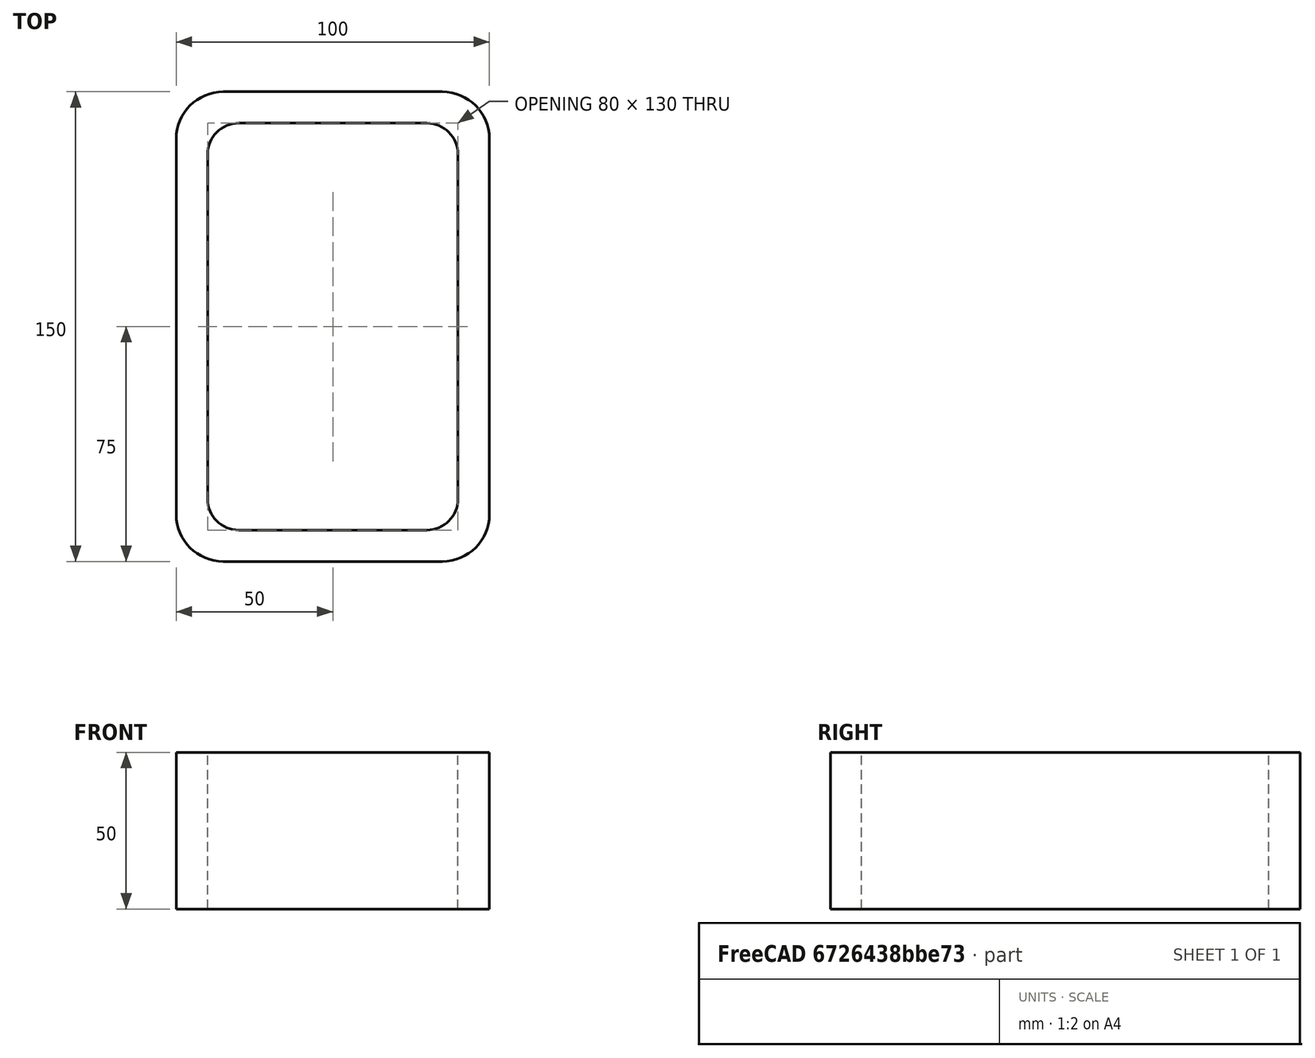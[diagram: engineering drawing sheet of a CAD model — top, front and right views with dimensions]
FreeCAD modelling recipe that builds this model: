
FCSTD DOCUMENT  (FreeCAD 0.15R4671 (Git))
Label: Rectangular hollow section 150x100x10 EN10219 S235JRH
License: All rights reserved
LicenseURL: http://en.wikipedia.org/wiki/All_rights_reserved
objects: Sketcher::SketchObject×1, Part::Extrusion×1
note: 2 computed .brp shape members not serialized (recipe doc carries the construction recipe); baked Part::Feature solids carry a one-line shape summary decoded from their .brp

FEATURE [Sketcher::SketchObject] Sketch
  sketch-geometry (16):
    g0: LineSegment StartX=-30 StartY=65 StartZ=0 EndX=30 EndY=65 EndZ=0
    g1: LineSegment StartX=40 StartY=55 StartZ=0 EndX=40 EndY=-55 EndZ=0
    g2: LineSegment StartX=30 StartY=-65 StartZ=0 EndX=-30 EndY=-65 EndZ=0
    g3: LineSegment StartX=-40 StartY=-55 StartZ=0 EndX=-40 EndY=55 EndZ=0
    g4: LineSegment StartX=-35 StartY=75 StartZ=0 EndX=35 EndY=75 EndZ=0
    g5: LineSegment StartX=50 StartY=60 StartZ=0 EndX=50 EndY=-60 EndZ=0
    g6: LineSegment StartX=35 StartY=-75 StartZ=0 EndX=-35 EndY=-75 EndZ=0
    g7: LineSegment StartX=-50 StartY=-60 StartZ=0 EndX=-50 EndY=60 EndZ=0
    g8: ArcOfCircle CenterX=-30 CenterY=55 CenterZ=0 NormalX=0 NormalY=0 NormalZ=1 Radius=10 StartAngle=1.5708 EndAngle=3.14159
    g9: ArcOfCircle CenterX=30 CenterY=55 CenterZ=0 NormalX=0 NormalY=0 NormalZ=1 Radius=10 StartAngle=0 EndAngle=1.5708
    g10: ArcOfCircle CenterX=30 CenterY=-55 CenterZ=0 NormalX=0 NormalY=0 NormalZ=1 Radius=10 StartAngle=4.71239 EndAngle=6.28319
    g11: ArcOfCircle CenterX=-30 CenterY=-55 CenterZ=0 NormalX=0 NormalY=0 NormalZ=1 Radius=10 StartAngle=3.14159 EndAngle=4.71239
    g12: ArcOfCircle CenterX=35 CenterY=60 CenterZ=0 NormalX=0 NormalY=0 NormalZ=1 Radius=15 StartAngle=0 EndAngle=1.5708
    g13: ArcOfCircle CenterX=35 CenterY=-60 CenterZ=0 NormalX=0 NormalY=0 NormalZ=1 Radius=15 StartAngle=4.71239 EndAngle=6.28319
    g14: ArcOfCircle CenterX=-35 CenterY=-60 CenterZ=0 NormalX=0 NormalY=0 NormalZ=1 Radius=15 StartAngle=3.14159 EndAngle=4.71239
    g15: ArcOfCircle CenterX=-35 CenterY=60 CenterZ=0 NormalX=0 NormalY=0 NormalZ=1 Radius=15 StartAngle=1.5708 EndAngle=3.14159
  constraints (36):
    c: Horizontal(g2)
    c: Vertical(g3)
    c: Horizontal(g6)
    c: Vertical(g7)
    c: Tangent(g3,g8) = 1.5708
    c: Tangent(g0,g8) = 1.5708
    c: Tangent(g0,g9) = 1.5708
    c: Tangent(g1,g9) = 1.5708
    c: Tangent(g1,g10) = 1.5708
    c: Tangent(g2,g10) = 1.5708
    c: Tangent(g2,g11) = 1.5708
    c: Tangent(g3,g11) = 1.5708
    c: Tangent(g4,g12) = 1.5708
    c: Tangent(g5,g12) = 1.5708
    c: Tangent(g5,g13) = 1.5708
    c: Tangent(g6,g13) = 1.5708
    c: Tangent(g6,g14) = 1.5708
    c: Tangent(g7,g14) = 1.5708
    c: Tangent(g7,g15) = 1.5708
    c: Tangent(g4,g15) = 1.5708
    c: Equal(g9,g8)
    c: Equal(g9,g11)
    c: Equal(g9,g10)
    c: Equal(g12,g15)
    c: Equal(g12,g14)
    c: Equal(g12,g13)
    c: Symmetric(g4,g6,g-1)
    c: Symmetric(g7,g5,g-2)
    c: DistanceY(g4,g6) = -150
    c: DistanceX(g7,g5) = 100
    c: Symmetric(g3,g1,g-2)
    c: Symmetric(g0,g2,g-1)
    c: DistanceY(g0,g4) = 10
    c: DistanceX(g5,g1) = -10
    c: Radius(g9) = 10
    c: Radius(g12) = 15
FEATURE [Part::Extrusion] Extrude  label="Rectangular hollow section 150x100x10 EN10219 S235JRH"
  Base = -> Sketch
  Dir = (0,0,50)
  Solid = true
